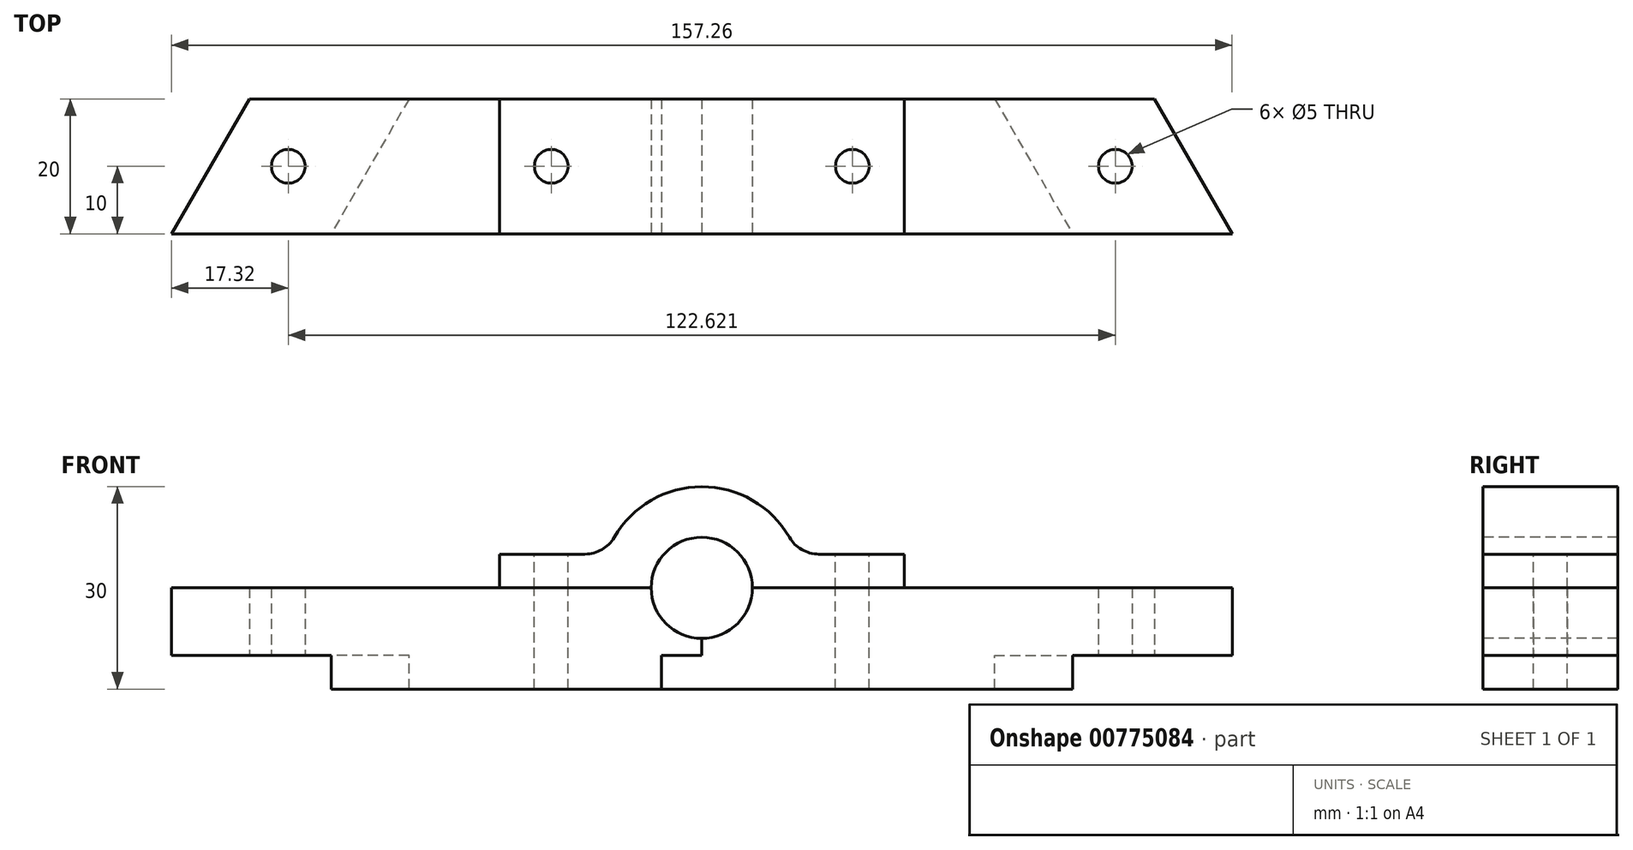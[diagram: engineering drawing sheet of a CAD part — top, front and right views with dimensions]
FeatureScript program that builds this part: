
annotation { "Feature Type Name" : "Feature", "Feature Type Description" : "" }
export const myFeature = defineFeature(function(context is Context, id is Id, definition is map)
    precondition{}
    {
        {
            var Q0;
            Q0=qCreatedBy(makeId("Top.planeOp"),FACE);
            var sketch = newSketch(context, id + "F0", { "sketchPlane" : qUnion([Q0])});
            skLineSegment(sketch, "E0", {"start": v(-75.06, -53.8) * mm, "end": v(0, 76.2) * mm, "construction": true});
            skLineSegment(sketch, "E1", {"start": v(0, 76.2) * mm, "end": v(75.06, -53.8) * mm, "construction": true});
            skLineSegment(sketch, "E2.0", {"start": v(-78.63, -40) * mm, "end": v(-67.08, -20) * mm});
            skLineSegment(sketch, "E3.0", {"start": v(67.08, -20) * mm, "end": v(78.63, -40) * mm});
            skLineSegment(sketch, "E4", {"start": v(-67.08, -20) * mm, "end": v(67.08, -20) * mm});
            skLineSegment(sketch, "E5", {"start": v(78.63, -40) * mm, "end": v(-78.63, -40) * mm});
            skSolve(sketch);
        }
        {
            var Q0;
            Q0 = qSketchRegion(id + "F0", true);
            extrude(context, id + "F1", {"entities" : qUnion([Q0]), "depth" : 10 * mm, "offsetDistance" : 25 * mm});
        }
        {
            var Q0;
            {var subQ0=sQuery(id+"F0.wireOp",EDGE,"E4");var subQ1=sQuery(id+"F0.wireOp",EDGE,"E5");var subQ2=sQuery(id+"F0.wireOp",EDGE,"E2.0");Q0=makeQuery(id+"FWpaCFhQHZ2rSSY_1.boolean.opBoolean","SPLIT",FACE,{"disambiguationData":[TD([makeQuery(id+"F1.opExtrude","SWEPT_FACE",FACE,{"disambiguationData":[OSD([subQ2])]})])],"derivedFrom":makeQuery(id+"F1.opExtrude","CAP_FACE",FACE,{"disambiguationData":[OSD([subQ2,sQuery(id+"F0.wireOp",EDGE,"E3.0"),subQ0,subQ1])],"isStart":true})});}
            var sketch = newSketch(context, id + "F2", { "sketchPlane" : qUnion([Q0])});
            skLineSegment(sketch, "E6.0", {"start": v(-69.97, 45) * mm, "end": v(-58.42, 25) * mm, "construction": true});
            skLineSegment(sketch, "E7.0", {"start": v(58.42, 25) * mm, "end": v(69.97, 45) * mm, "construction": true});
            skLineSegment(sketch, "E8", {"start": v(-61.31, 30) * mm, "end": v(61.31, 30) * mm, "construction": true});
            skPoint(sketch, "E8.startSnap0", {"position": v(-44, 30) * mm});
            skCircle(sketch, "E9", {"center": v(-61.31, 30) * mm, "radius": 2.5 * mm});
            skCircle(sketch, "E10", {"center": v(61.31, 30) * mm, "radius": 2.5 * mm});
            skSolve(sketch);
        }
        {
            var Q0;
            Q0 = qSketchRegion(id + "F2", true);
            extrude(context, id + "F3", {"entities" : qUnion([Q0]), "operationType" : NewBodyOperationType.REMOVE, "oppositeDirection" : true, "depth" : 10 * mm, "offsetDistance" : 25 * mm});
        }
        {
            var Q0;
            Q0=makeQuery(id+"F1.opExtrude","CAP_FACE",FACE,{"disambiguationData":[OSD([sQuery(id+"F0.wireOp",EDGE,"E2.0"),sQuery(id+"F0.wireOp",EDGE,"E3.0"),sQuery(id+"F0.wireOp",EDGE,"E4"),sQuery(id+"F0.wireOp",EDGE,"E5")])],"isStart":true});
            var sketch = newSketch(context, id + "F4", { "sketchPlane" : qUnion([Q0])});
            skLineSegment(sketch, "E11.0", {"start": v(-54.96, 40) * mm, "end": v(-43.41, 20) * mm});
            skLineSegment(sketch, "E12.0", {"start": v(43.41, 20) * mm, "end": v(54.96, 40) * mm});
            skLineSegment(sketch, "E13", {"start": v(-54.96, 40) * mm, "end": v(54.96, 40) * mm});
            skLineSegment(sketch, "E14", {"start": v(-43.41, 20) * mm, "end": v(43.41, 20) * mm});
            skSolve(sketch);
        }
        {
            var Q0;
            Q0 = qSketchRegion(id + "F4", true);
            extrude(context, id + "F5", {"entities" : qUnion([Q0]), "operationType" : NewBodyOperationType.ADD, "depth" : 5 * mm, "offsetDistance" : 25 * mm});
        }
        {
            var Q0;
            Q0=makeQuery(id+"F5.boolean.opBoolean","MERGE",FACE,{"derivedFrom":[makeQuery(id+"F1.opExtrude","SWEPT_FACE",FACE,{"disambiguationData":[OSD([sQuery(id+"F0.wireOp",EDGE,"E5")])]}),makeQuery(id+"F5.opExtrude","SWEPT_FACE",FACE,{"disambiguationData":[OSD([sQuery(id+"F4.wireOp",EDGE,"E13")])]})]});
            var sketch = newSketch(context, id + "F6", { "sketchPlane" : qUnion([Q0])});
            skArc(sketch, "E15", {"start": v(14.14, 15) * mm, "mid": v(0, 25) * mm, "end": v(-14.14, 15) * mm});
            skLineSegment(sketch, "E16", {"start": v(-30, 15) * mm, "end": v(-14.14, 15) * mm});
            skLineSegment(sketch, "E17", {"start": v(30, 15) * mm, "end": v(30, 10) * mm});
            skLineSegment(sketch, "E18", {"start": v(30, 10) * mm, "end": v(-30, 10) * mm});
            skLineSegment(sketch, "E19", {"start": v(-30, 10) * mm, "end": v(-30, 15) * mm});
            skLineSegment(sketch, "E20.trimOffspring", {"start": v(14.14, 15) * mm, "end": v(30, 15) * mm});
            skSolve(sketch);
        }
        {
            var Q0;
            Q0 = qSketchRegion(id + "F6", true);
            var Q1;
            Q1=makeQuery(id+"F5.boolean.opBoolean","MERGE",FACE,{"derivedFrom":[makeQuery(id+"F1.opExtrude","SWEPT_FACE",FACE,{"disambiguationData":[OSD([sQuery(id+"F0.wireOp",EDGE,"E4")])]}),makeQuery(id+"F5.opExtrude","SWEPT_FACE",FACE,{"disambiguationData":[OSD([sQuery(id+"F4.wireOp",EDGE,"E14")])]})]});
            extrude(context, id + "F7", {"entities" : qUnion([Q0]), "endBound" : BoundingType.UP_TO_SURFACE, "oppositeDirection" : true, "depth" : 25 * mm, "endBoundEntityFace" : qUnion([Q1]), "offsetDistance" : 25 * mm});
        }
        {
            var Q0;
            Q0=makeQuery(id+"F7.opExtrude","CAP_FACE",FACE,{"disambiguationData":[OSD([sQuery(id+"F6.wireOp",EDGE,"E15"),sQuery(id+"F6.wireOp",EDGE,"E16"),sQuery(id+"F6.wireOp",EDGE,"E17"),sQuery(id+"F6.wireOp",EDGE,"E18"),sQuery(id+"F6.wireOp",EDGE,"E19"),sQuery(id+"F6.wireOp",EDGE,"E20.trimOffspring")])],"isStart":true});
            var sketch = newSketch(context, id + "F8", { "sketchPlane" : qUnion([Q0])});
            skCircle(sketch, "E21", {"center": v(0, 10) * mm, "radius": 7.5 * mm});
            skSolve(sketch);
        }
        {
            var Q0;
            Q0 = qSketchRegion(id + "F8", true);
            extrude(context, id + "F9", {"entities" : qUnion([Q0]), "operationType" : NewBodyOperationType.REMOVE, "oppositeDirection" : true, "depth" : 25 * mm, "offsetDistance" : 25 * mm});
        }
        {
            var Q0;
            Q0=makeQuery(id+"F7.opExtrude","SWEPT_EDGE",EDGE,{"disambiguationData":[OSD([sQuery(id+"F6.wireOp",EDGE,"E15"),sQuery(id+"F6.wireOp",EDGE,"E20.trimOffspring")])]});
            var Q1;
            Q1=makeQuery(id+"F7.opExtrude","SWEPT_EDGE",EDGE,{"disambiguationData":[OSD([sQuery(id+"F6.wireOp",EDGE,"E15"),sQuery(id+"F6.wireOp",EDGE,"E16")])]});
            fillet(context, id + "F10", {"entities" : qUnion([Q0, Q1]), "radius" : 5 * mm, "tangentPropagation" : true, "allowEdgeOverflow" : false});
        }
        {
            var Q0;
            Q0=makeQuery(id+"F1.opExtrude","SWEPT_BODY",BODY,{"disambiguationData":[OSD([sQuery(id+"F0.wireOp",EDGE,"E2.0"),sQuery(id+"F0.wireOp",EDGE,"E3.0"),sQuery(id+"F0.wireOp",EDGE,"E4"),sQuery(id+"F0.wireOp",EDGE,"E5")])]});
            transform(context, id + "F11", {"entities" : qUnion([Q0]), "transformType" : TransformType.TRANSLATION_3D, "dx" : 201 * mm, "dy" : 0 * mm, "dz" : 0 * mm, "makeCopy" : true});
        }
        {
            var Q0;
            Q0=makeQuery(id+"F11.opPattern","COPY",FACE,{"derivedFrom":makeQuery(id+"F5.boolean.opBoolean","MERGE",FACE,{"derivedFrom":[makeQuery(id+"F1.opExtrude","SWEPT_FACE",FACE,{"disambiguationData":[OSD([sQuery(id+"F0.wireOp",EDGE,"E5")])]}),makeQuery(id+"F5.opExtrude","SWEPT_FACE",FACE,{"disambiguationData":[OSD([sQuery(id+"F4.wireOp",EDGE,"E13")])]})]}),"instanceName":"1"});
            var sketch = newSketch(context, id + "F12", { "sketchPlane" : qUnion([Q0])});
            skLineSegment(sketch, "E22", {"start": v(201, 2.5) * mm, "end": v(201, -5) * mm});
            skLineSegment(sketch, "E23", {"start": v(201, -5) * mm, "end": v(146.04, -5) * mm});
            skLineSegment(sketch, "E24", {"start": v(146.04, -5) * mm, "end": v(146.04, 0) * mm});
            skLineSegment(sketch, "E25", {"start": v(146.04, 0) * mm, "end": v(122.37, 0) * mm});
            skLineSegment(sketch, "E26", {"start": v(122.37, 0) * mm, "end": v(122.37, 10) * mm});
            skLineSegment(sketch, "E27", {"start": v(122.37, 10) * mm, "end": v(201, 10) * mm});
            skLineSegment(sketch, "E28", {"start": v(201, 10) * mm, "end": v(201, 2.5) * mm});
            skSolve(sketch);
        }
        {
            var Q0;
            Q0 = qSketchRegion(id + "F12", true);
            extrude(context, id + "F13", {"entities" : qUnion([Q0]), "operationType" : NewBodyOperationType.REMOVE, "oppositeDirection" : true, "depth" : 25 * mm, "offsetDistance" : 25 * mm});
        }
        {
            var Q0;
            Q0=makeQuery(id+"F11.opPattern","COPY",BODY,{"derivedFrom":makeQuery(id+"F1.opExtrude","SWEPT_BODY",BODY,{"disambiguationData":[OSD([sQuery(id+"F0.wireOp",EDGE,"E2.0"),sQuery(id+"F0.wireOp",EDGE,"E3.0"),sQuery(id+"F0.wireOp",EDGE,"E4"),sQuery(id+"F0.wireOp",EDGE,"E5")])]}),"instanceName":"1"});
            var Q1;
            Q1=makeQuery(id+"F13.boolean.opBoolean","COPY",FACE,{"derivedFrom":makeQuery(id+"F13.opExtrude","SWEPT_FACE",FACE,{"disambiguationData":[OSD([sQuery(id+"F12.wireOp",EDGE,"E22"),sQuery(id+"F12.wireOp",EDGE,"E28")])]})});
            mirror(context, id + "F14", {"entities" : qUnion([Q0]), "mirrorPlane" : qUnion([Q1])});
        }
        {
            var Q0;
            Q0=makeQuery(id+"F14.opPattern","COPY",BODY,{"derivedFrom":makeQuery(id+"F11.opPattern","COPY",BODY,{"derivedFrom":makeQuery(id+"F1.opExtrude","SWEPT_BODY",BODY,{"disambiguationData":[OSD([sQuery(id+"F0.wireOp",EDGE,"E2.0"),sQuery(id+"F0.wireOp",EDGE,"E3.0"),sQuery(id+"F0.wireOp",EDGE,"E4"),sQuery(id+"F0.wireOp",EDGE,"E5")])]}),"instanceName":"1"}),"instanceName":"1"});
            var Q1;
            Q1=makeQuery(id+"F14.opPattern","COPY",EDGE,{"derivedFrom":makeQuery(id+"F11.opPattern","COPY",EDGE,{"derivedFrom":makeQuery(id+"F5.opExtrude","CAP_EDGE",EDGE,{"disambiguationData":[OSD([sQuery(id+"F4.wireOp",EDGE,"E13")])],"isStart":false}),"instanceName":"1"}),"instanceName":"1"});
            var Q2;
            Q2=makeQuery(id+"F14.opPattern","COPY",EDGE,{"derivedFrom":makeQuery(id+"F11.opPattern","COPY",EDGE,{"derivedFrom":makeQuery(id+"F5.opExtrude","CAP_EDGE",EDGE,{"disambiguationData":[OSD([sQuery(id+"F4.wireOp",EDGE,"E13")])],"isStart":false}),"instanceName":"1"}),"instanceName":"1"});
            transform(context, id + "F15", {"entities" : qUnion([Q0]), "transformType" : TransformType.TRANSLATION_DISTANCE, "transformDirection" : qUnion([Q2]), "distance" : 13.6 * mm, "oppositeDirection" : true, "makeCopy" : false});
        }
        {
            var Q0;
            Q0=makeQuery(id+"F14.opPattern","COPY",FACE,{"derivedFrom":makeQuery(id+"F11.opPattern","COPY",FACE,{"derivedFrom":makeQuery(id+"F5.boolean.opBoolean","MERGE",FACE,{"derivedFrom":[makeQuery(id+"F1.opExtrude","SWEPT_FACE",FACE,{"disambiguationData":[OSD([sQuery(id+"F0.wireOp",EDGE,"E5")])]}),makeQuery(id+"F5.opExtrude","SWEPT_FACE",FACE,{"disambiguationData":[OSD([sQuery(id+"F4.wireOp",EDGE,"E13")])]})]}),"instanceName":"1"}),"instanceName":"1"});
            var sketch = newSketch(context, id + "F16", { "sketchPlane" : qUnion([Q0])});
            skLineSegment(sketch, "E29.bottom", {"start": v(187.4, 0) * mm, "end": v(181.4, 0) * mm});
            skLineSegment(sketch, "E29.top", {"start": v(187.4, -5) * mm, "end": v(181.4, -5) * mm});
            skLineSegment(sketch, "E29.left", {"start": v(187.4, 0) * mm, "end": v(187.4, -5) * mm});
            skLineSegment(sketch, "E29.right", {"start": v(181.4, 0) * mm, "end": v(181.4, -5) * mm});
            skSolve(sketch);
        }
        {
            var Q0;
            Q0 = qSketchRegion(id + "F16", true);
            extrude(context, id + "F17", {"entities" : qUnion([Q0]), "operationType" : NewBodyOperationType.REMOVE, "endBound" : BoundingType.THROUGH_ALL, "oppositeDirection" : true, "depth" : 25 * mm, "offsetDistance" : 25 * mm});
        }
        {
            var Q0;
            Q0=makeQuery(id+"F11.opPattern","COPY",FACE,{"derivedFrom":makeQuery(id+"F5.boolean.opBoolean","MERGE",FACE,{"derivedFrom":[makeQuery(id+"F1.opExtrude","SWEPT_FACE",FACE,{"disambiguationData":[OSD([sQuery(id+"F0.wireOp",EDGE,"E5")])]}),makeQuery(id+"F5.opExtrude","SWEPT_FACE",FACE,{"disambiguationData":[OSD([sQuery(id+"F4.wireOp",EDGE,"E13")])]})]}),"instanceName":"1"});
            var sketch = newSketch(context, id + "F18", { "sketchPlane" : qUnion([Q0])});
            skLineSegment(sketch, "E30.bottom", {"start": v(201, 0) * mm, "end": v(195, 0) * mm});
            skLineSegment(sketch, "E30.top", {"start": v(201, -5) * mm, "end": v(195, -5) * mm});
            skLineSegment(sketch, "E30.left", {"start": v(201, 0) * mm, "end": v(201, -5) * mm});
            skLineSegment(sketch, "E30.right", {"start": v(195, 0) * mm, "end": v(195, -5) * mm});
            skSolve(sketch);
        }
        {
            var Q0;
            Q0 = qSketchRegion(id + "F18", true);
            var Q1;
            Q1=makeQuery(id+"F11.opPattern","COPY",FACE,{"derivedFrom":makeQuery(id+"F5.boolean.opBoolean","MERGE",FACE,{"derivedFrom":[makeQuery(id+"F1.opExtrude","SWEPT_FACE",FACE,{"disambiguationData":[OSD([sQuery(id+"F0.wireOp",EDGE,"E4")])]}),makeQuery(id+"F5.opExtrude","SWEPT_FACE",FACE,{"disambiguationData":[OSD([sQuery(id+"F4.wireOp",EDGE,"E14")])]})]}),"instanceName":"1"});
            extrude(context, id + "F19", {"entities" : qUnion([Q0]), "operationType" : NewBodyOperationType.ADD, "endBound" : BoundingType.UP_TO_SURFACE, "oppositeDirection" : true, "depth" : 25 * mm, "endBoundEntityFace" : qUnion([Q1]), "offsetDistance" : 25 * mm});
        }
        {
            var Q0;
            Q0=makeQuery(id+"F1.opExtrude","SWEPT_BODY",BODY,{"disambiguationData":[OSD([sQuery(id+"F0.wireOp",EDGE,"E2.0"),sQuery(id+"F0.wireOp",EDGE,"E3.0"),sQuery(id+"F0.wireOp",EDGE,"E4"),sQuery(id+"F0.wireOp",EDGE,"E5")])]});
            deleteBodies(context, id + "F20", {"entities" : qUnion([Q0])});
        }
        {
            var Q0;
            Q0=makeQuery(id+"F14.opPattern","COPY",BODY,{"derivedFrom":makeQuery(id+"F11.opPattern","COPY",BODY,{"derivedFrom":makeQuery(id+"F1.opExtrude","SWEPT_BODY",BODY,{"disambiguationData":[OSD([sQuery(id+"F0.wireOp",EDGE,"E2.0"),sQuery(id+"F0.wireOp",EDGE,"E3.0"),sQuery(id+"F0.wireOp",EDGE,"E4"),sQuery(id+"F0.wireOp",EDGE,"E5")])]}),"instanceName":"1"}),"instanceName":"1"});
            var Q1;
            Q1=makeQuery(id+"F14.opPattern","COPY",EDGE,{"derivedFrom":makeQuery(id+"F11.opPattern","COPY",EDGE,{"derivedFrom":makeQuery(id+"F5.opExtrude","CAP_EDGE",EDGE,{"disambiguationData":[OSD([sQuery(id+"F4.wireOp",EDGE,"E13")])],"isStart":false}),"instanceName":"1"}),"instanceName":"1"});
            transform(context, id + "F21", {"entities" : qUnion([Q0]), "transformType" : TransformType.TRANSLATION_DISTANCE, "transformDirection" : qUnion([Q1]), "distance" : 187 * mm, "oppositeDirection" : true, "makeCopy" : false});
        }
        {
            var Q0;
            Q0=makeQuery(id+"F14.opPattern","COPY",BODY,{"derivedFrom":makeQuery(id+"F11.opPattern","COPY",BODY,{"derivedFrom":makeQuery(id+"F1.opExtrude","SWEPT_BODY",BODY,{"disambiguationData":[OSD([sQuery(id+"F0.wireOp",EDGE,"E2.0"),sQuery(id+"F0.wireOp",EDGE,"E3.0"),sQuery(id+"F0.wireOp",EDGE,"E4"),sQuery(id+"F0.wireOp",EDGE,"E5")])]}),"instanceName":"1"}),"instanceName":"1"});
            var Q1;
            {var subQ0=sQuery(id+"F0.wireOp",EDGE,"E5");var subQ1=sQuery(id+"F0.wireOp",EDGE,"E3.0");Q1=makeQuery(id+"F14.opPattern","COPY",EDGE,{"derivedFrom":makeQuery(id+"F11.opPattern","COPY",EDGE,{"derivedFrom":makeQuery(id+"F9.boolean.opBoolean","SPLIT",EDGE,{"disambiguationData":[TD([makeQuery(id+"F1.opExtrude","SWEPT_FACE",FACE,{"disambiguationData":[OSD([subQ1])]})])],"derivedFrom":makeQuery(id+"F1.opExtrude","CAP_EDGE",EDGE,{"disambiguationData":[OSD([subQ0])],"isStart":false})}),"instanceName":"1"}),"instanceName":"1"});}
            transform(context, id + "F22", {"entities" : qUnion([Q0]), "transformType" : TransformType.TRANSLATION_DISTANCE, "transformDirection" : qUnion([Q1]), "distance" : .5 * mm, "oppositeDirection" : true, "makeCopy" : false});
        }
        {
            var Q0;
            Q0=makeQuery(id+"F11.opPattern","COPY",BODY,{"derivedFrom":makeQuery(id+"F1.opExtrude","SWEPT_BODY",BODY,{"disambiguationData":[OSD([sQuery(id+"F0.wireOp",EDGE,"E2.0"),sQuery(id+"F0.wireOp",EDGE,"E3.0"),sQuery(id+"F0.wireOp",EDGE,"E4"),sQuery(id+"F0.wireOp",EDGE,"E5")])]}),"instanceName":"1"});
            var Q1;
            Q1=makeQuery(id+"F19.boolean.opBoolean","MERGE",EDGE,{"derivedFrom":[makeQuery(id+"F11.opPattern","COPY",EDGE,{"derivedFrom":makeQuery(id+"F5.opExtrude","CAP_EDGE",EDGE,{"disambiguationData":[OSD([sQuery(id+"F4.wireOp",EDGE,"E13")])],"isStart":false}),"instanceName":"1"}),makeQuery(id+"F19.opExtrude","CAP_EDGE",EDGE,{"disambiguationData":[OSD([sQuery(id+"F18.wireOp",EDGE,"E30.top")])],"isStart":true})]});
            transform(context, id + "F23", {"entities" : qUnion([Q0]), "transformType" : TransformType.TRANSLATION_DISTANCE, "transformDirection" : qUnion([Q1]), "distance" : 200 * mm, "makeCopy" : false});
        }
        {
            var Q0;
            Q0=makeQuery(id+"F11.opPattern","COPY",BODY,{"derivedFrom":makeQuery(id+"F1.opExtrude","SWEPT_BODY",BODY,{"disambiguationData":[OSD([sQuery(id+"F0.wireOp",EDGE,"E2.0"),sQuery(id+"F0.wireOp",EDGE,"E3.0"),sQuery(id+"F0.wireOp",EDGE,"E4"),sQuery(id+"F0.wireOp",EDGE,"E5")])]}),"instanceName":"1"});
            var Q1;
            Q1=qCreatedBy(makeId("Origin.pointOp"),VERTEX);
            var Q2;
            Q2=makeQuery(id+"F19.boolean.opBoolean","MERGE",EDGE,{"derivedFrom":[makeQuery(id+"F11.opPattern","COPY",EDGE,{"derivedFrom":makeQuery(id+"F5.opExtrude","CAP_EDGE",EDGE,{"disambiguationData":[OSD([sQuery(id+"F4.wireOp",EDGE,"E13")])],"isStart":false}),"instanceName":"1"}),makeQuery(id+"F19.opExtrude","CAP_EDGE",EDGE,{"disambiguationData":[OSD([sQuery(id+"F18.wireOp",EDGE,"E30.top")])],"isStart":true})]});
            transform(context, id + "F24", {"entities" : qUnion([Q0]), "transformType" : TransformType.TRANSLATION_DISTANCE, "transformDirection" : qUnion([Q2]), "distance" : 1 * mm, "makeCopy" : false});
        }
        {
            var Q0;
            Q0=makeQuery(id+"F14.opPattern","COPY",BODY,{"derivedFrom":makeQuery(id+"F11.opPattern","COPY",BODY,{"derivedFrom":makeQuery(id+"F1.opExtrude","SWEPT_BODY",BODY,{"disambiguationData":[OSD([sQuery(id+"F0.wireOp",EDGE,"E2.0"),sQuery(id+"F0.wireOp",EDGE,"E3.0"),sQuery(id+"F0.wireOp",EDGE,"E4"),sQuery(id+"F0.wireOp",EDGE,"E5")])]}),"instanceName":"1"}),"instanceName":"1"});
            var Q1;
            Q1=makeQuery(id+"F14.opPattern","COPY",EDGE,{"derivedFrom":makeQuery(id+"F11.opPattern","COPY",EDGE,{"derivedFrom":makeQuery(id+"F5.opExtrude","CAP_EDGE",EDGE,{"disambiguationData":[OSD([sQuery(id+"F4.wireOp",EDGE,"E13")])],"isStart":false}),"instanceName":"1"}),"instanceName":"1"});
            var Q2;
            Q2=qCreatedBy(makeId("Front.planeOp"),FACE);
            transform(context, id + "F25", {"entities" : qUnion([Q0]), "transformType" : TransformType.TRANSLATION_DISTANCE, "transformDirection" : qUnion([Q1, Q2]), "distance" : .1 * mm, "makeCopy" : false});
        }
        {
            var Q0;
            Q0=makeQuery(id+"F7.opExtrude","SWEPT_FACE",FACE,{"disambiguationData":[OSD([sQuery(id+"F6.wireOp",EDGE,"E20.trimOffspring")])]});
            var sketch = newSketch(context, id + "F26", { "sketchPlane" : qUnion([Q0])});
            skCircle(sketch, "E31", {"center": v(-22.32, -30) * mm, "radius": 2.5 * mm});
            skCircle(sketch, "E32", {"center": v(22.32, -30) * mm, "radius": 2.5 * mm});
            skPoint(sketch, "E32.centerSnap0", {"position": v(17.32, -30) * mm});
            skSolve(sketch);
        }
        {
            var Q0;
            Q0 = qSketchRegion(id + "F26", true);
            extrude(context, id + "F27", {"entities" : qUnion([Q0]), "operationType" : NewBodyOperationType.REMOVE, "endBound" : BoundingType.THROUGH_ALL, "oppositeDirection" : true, "depth" : 25 * mm, "offsetDistance" : 25 * mm});
        }
    });
